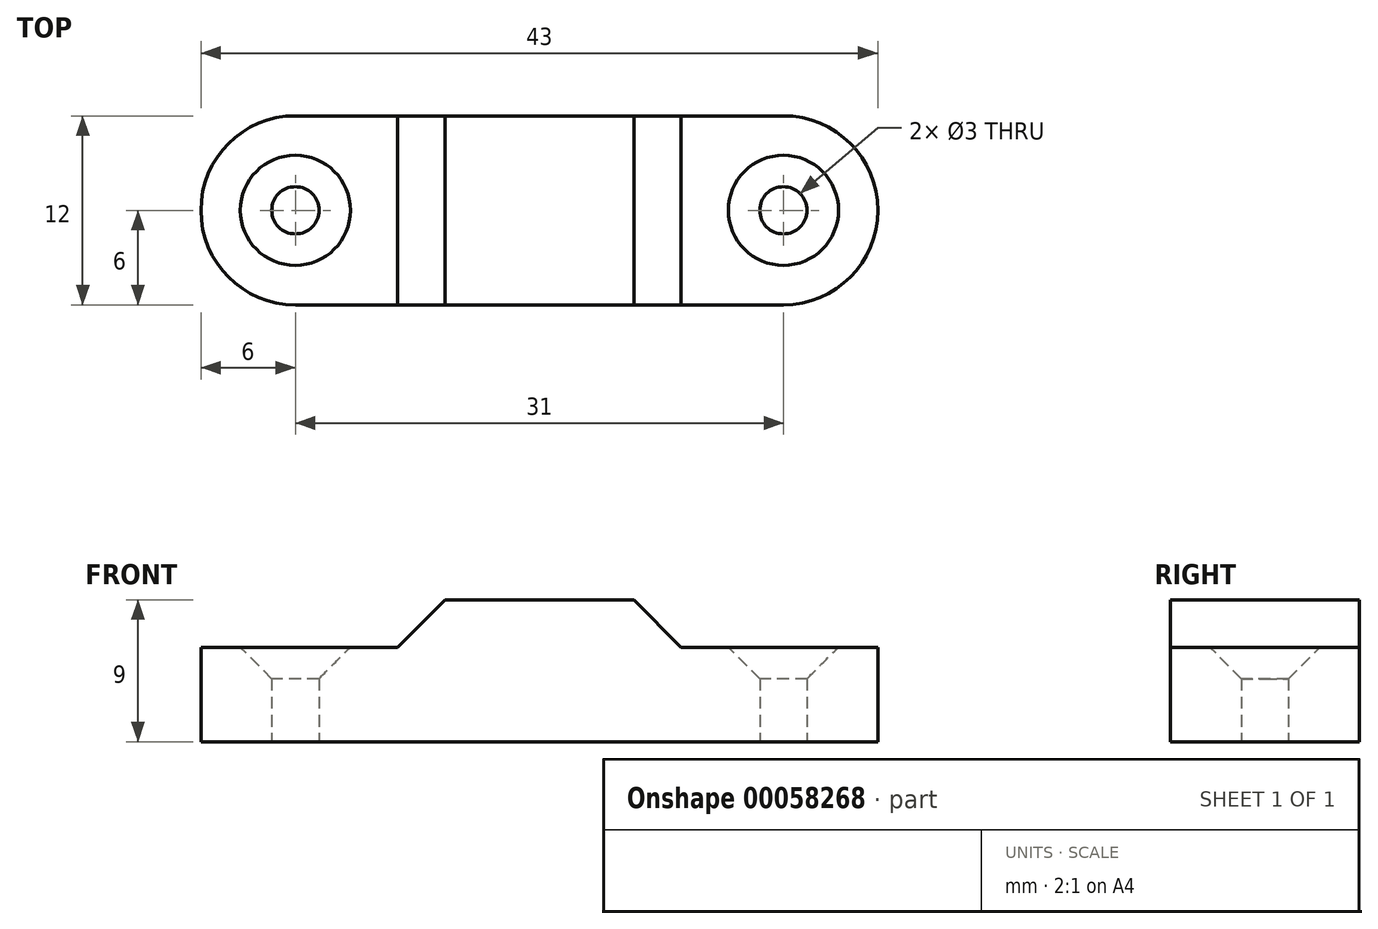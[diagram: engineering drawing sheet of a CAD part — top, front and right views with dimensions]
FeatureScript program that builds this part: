
annotation { "Feature Type Name" : "Feature", "Feature Type Description" : "" }
export const myFeature = defineFeature(function(context is Context, id is Id, definition is map)
    precondition{}
    {
        {
            var Q0;
            Q0=qCreatedBy(makeId("Top.planeOp"),FACE);
            var sketch = newSketch(context, id + "F0", { "sketchPlane" : qUnion([Q0])});
            skLineSegment(sketch, "E0", {"start": v(0, 0) * mm, "end": v(15.5, 0) * mm, "construction": true});
            skCircle(sketch, "E1", {"center": v(15.5, 0) * mm, "radius": 1.5 * mm});
            skLineSegment(sketch, "E2.bottom", {"start": v(21.5, 6) * mm, "end": v(-21.5, 6) * mm});
            skLineSegment(sketch, "E2.top", {"start": v(21.5, -6) * mm, "end": v(-21.5, -6) * mm});
            skLineSegment(sketch, "E2.left", {"start": v(21.5, 6) * mm, "end": v(21.5, -6) * mm});
            skLineSegment(sketch, "E2.right", {"start": v(-21.5, 6) * mm, "end": v(-21.5, -6) * mm});
            skPoint(sketch, "E2.middle", {"position": v(0, 0) * mm});
            skLineSegment(sketch, "E3", {"start": v(0, 6) * mm, "end": v(0, 0) * mm, "construction": true});
            skCircle(sketch, "E4.MirrorC", {"center": v(-15.5, 0) * mm, "radius": 1.5 * mm});
            skSolve(sketch);
        }
        {
            var Q0;
            Q0 = qSketchRegion(id + "F0", true);
            extrude(context, id + "F1", {"entities" : qUnion([Q0]), "depth" : 6 * mm});
        }
        {
            var Q0;
            Q0=makeQuery(id+"F1.opExtrude","SWEPT_EDGE",EDGE,{"disambiguationData":[OSD([sQuery(id+"F0.wireOp",EDGE,"E2.bottom"),sQuery(id+"F0.wireOp",EDGE,"E2.right")])]});
            var Q1;
            Q1=makeQuery(id+"F1.opExtrude","SWEPT_EDGE",EDGE,{"disambiguationData":[OSD([sQuery(id+"F0.wireOp",EDGE,"E2.top"),sQuery(id+"F0.wireOp",EDGE,"E2.right")])]});
            var Q2;
            Q2=makeQuery(id+"F1.opExtrude","SWEPT_EDGE",EDGE,{"disambiguationData":[OSD([sQuery(id+"F0.wireOp",EDGE,"E2.top"),sQuery(id+"F0.wireOp",EDGE,"E2.left")])]});
            var Q3;
            Q3=makeQuery(id+"F1.opExtrude","SWEPT_EDGE",EDGE,{"disambiguationData":[OSD([sQuery(id+"F0.wireOp",EDGE,"E2.bottom"),sQuery(id+"F0.wireOp",EDGE,"E2.left")])]});
            fillet(context, id + "F2", {"entities" : qUnion([Q0, Q1, Q2, Q3]), "radius" : 6 * mm, "tangentPropagation" : true, "allowEdgeOverflow" : false});
        }
        {
            var Q0;
            Q0=makeQuery(id+"F1.opExtrude","CAP_EDGE",EDGE,{"disambiguationData":[OSD([sQuery(id+"F0.wireOp",EDGE,"E4.MirrorC")])],"isStart":false});
            var Q1;
            Q1=makeQuery(id+"F1.opExtrude","CAP_EDGE",EDGE,{"disambiguationData":[OSD([sQuery(id+"F0.wireOp",EDGE,"E1")])],"isStart":false});
            chamfer(context, id + "F3", {"entities" : qUnion([Q0, Q1]), "width" : 2 * mm, "tangentPropagation" : true});
        }
        {
            var Q0;
            Q0=makeQuery(id+"F1.opExtrude","CAP_FACE",FACE,{"disambiguationData":[OSD([sQuery(id+"F0.wireOp",EDGE,"E1"),sQuery(id+"F0.wireOp",EDGE,"E2.bottom"),sQuery(id+"F0.wireOp",EDGE,"E2.top"),sQuery(id+"F0.wireOp",EDGE,"E2.left"),sQuery(id+"F0.wireOp",EDGE,"E2.right"),sQuery(id+"F0.wireOp",EDGE,"E4.MirrorC")])],"isStart":false});
            extrude(context, id + "F4", {"entities" : qUnion([Q0]), "operationType" : NewBodyOperationType.ADD, "depth" : 3 * mm});
        }
        {
            var Q0;
            Q0=makeQuery(id+"F4.opExtrude","CAP_FACE",FACE,{"disambiguationData":[OSD([sQuery(id+"F0.wireOp",EDGE,"E1"),sQuery(id+"F0.wireOp",EDGE,"E2.bottom"),sQuery(id+"F0.wireOp",EDGE,"E2.top"),sQuery(id+"F0.wireOp",EDGE,"E2.left"),sQuery(id+"F0.wireOp",EDGE,"E2.right"),sQuery(id+"F0.wireOp",EDGE,"E4.MirrorC")])],"isStart":false});
            var sketch = newSketch(context, id + "F5", { "sketchPlane" : qUnion([Q0])});
            skLineSegment(sketch, "E5", {"start": v(0, 0) * mm, "end": v(0, 6) * mm, "construction": true});
            skArc(sketch, "E6.0", {"start": v(-15.5, 6) * mm, "mid": v(-21.5, 0) * mm, "end": v(-15.5, -6) * mm});
            skLineSegment(sketch, "E7", {"start": v(-15.5, 6) * mm, "end": v(-6, 6) * mm});
            skLineSegment(sketch, "E8", {"start": v(-6, 6) * mm, "end": v(-6, -6) * mm});
            skLineSegment(sketch, "E9", {"start": v(-6, -6) * mm, "end": v(-15.5, -6) * mm});
            skLineSegment(sketch, "E10.MirrorCS", {"start": v(6, -6) * mm, "end": v(15.5, -6) * mm});
            skLineSegment(sketch, "E11.MirrorCS", {"start": v(6, 6) * mm, "end": v(6, -6) * mm});
            skLineSegment(sketch, "E12.MirrorCS", {"start": v(15.5, 6) * mm, "end": v(6, 6) * mm});
            skArc(sketch, "E13.MirrorCS", {"start": v(15.5, 6) * mm, "mid": v(21.5, 0) * mm, "end": v(15.5, -6) * mm});
            skSolve(sketch);
        }
        {
            var Q0;
            Q0 = qSketchRegion(id + "F5", true);
            extrude(context, id + "F6", {"entities" : qUnion([Q0]), "operationType" : NewBodyOperationType.REMOVE, "oppositeDirection" : true, "depth" : 3 * mm});
        }
        {
            var Q0;
            Q0=makeQuery(id+"F6.boolean.opBoolean","COPY",EDGE,{"derivedFrom":makeQuery(id+"F6.opExtrude","CAP_EDGE",EDGE,{"disambiguationData":[OSD([sQuery(id+"F5.wireOp",EDGE,"E8")])],"isStart":false})});
            var Q1;
            Q1=makeQuery(id+"F6.boolean.opBoolean","COPY",EDGE,{"derivedFrom":makeQuery(id+"F6.opExtrude","CAP_EDGE",EDGE,{"disambiguationData":[OSD([sQuery(id+"F5.wireOp",EDGE,"E11.MirrorCS")])],"isStart":false})});
            chamfer(context, id + "F7", {"entities" : qUnion([Q0, Q1]), "width" : 3 * mm, "tangentPropagation" : true});
        }
    });
